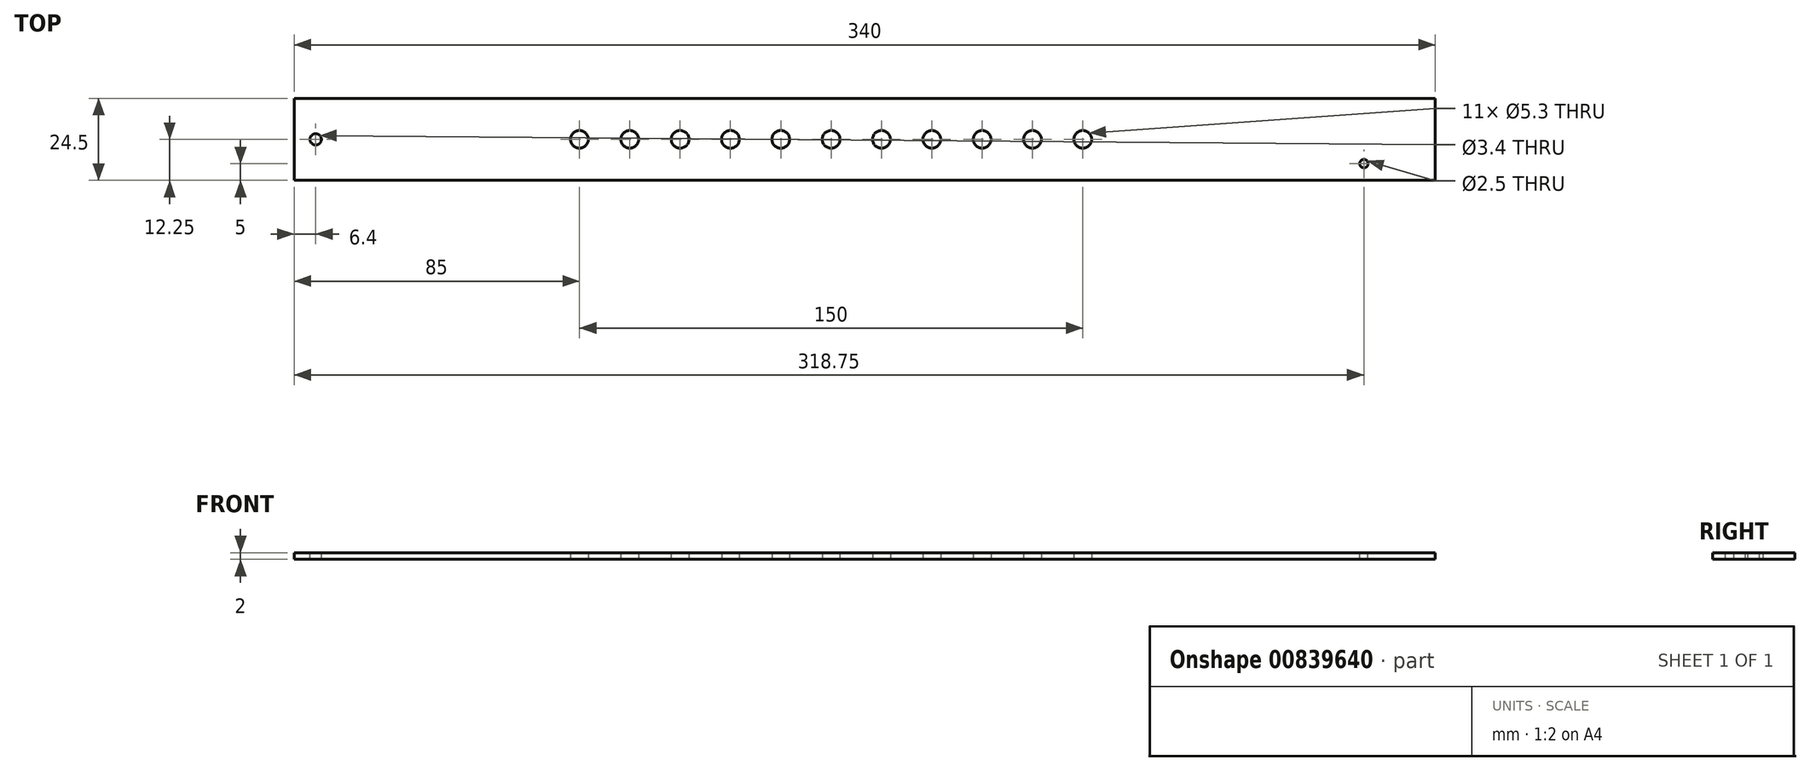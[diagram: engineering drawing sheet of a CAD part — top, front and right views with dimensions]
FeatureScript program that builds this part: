
annotation { "Feature Type Name" : "Feature", "Feature Type Description" : "" }
export const myFeature = defineFeature(function(context is Context, id is Id, definition is map)
    precondition{}
    {
        {
            var Q0;
            Q0=qCreatedBy(makeId("Top.planeOp"),FACE);
            var sketch = newSketch(context, id + "F0", { "sketchPlane" : qUnion([Q0])});
            skLineSegment(sketch, "E0.bottom", {"start": v(150, -12.25) * mm, "end": v(-150, -12.25) * mm});
            skLineSegment(sketch, "E0.top", {"start": v(150, 12.25) * mm, "end": v(-150, 12.25) * mm});
            skLineSegment(sketch, "E0.left", {"start": v(150, -12.25) * mm, "end": v(150, 12.25) * mm});
            skLineSegment(sketch, "E0.right", {"start": v(-150, -12.25) * mm, "end": v(-150, 12.25) * mm});
            skPoint(sketch, "E0.middle", {"position": v(0, 0) * mm});
            skCircle(sketch, "E1.4.0.0", {"center": v(-75, 0) * mm, "radius": 2.65 * mm});
            skCircle(sketch, "E1.5.0.0", {"center": v(-60, 0) * mm, "radius": 2.65 * mm});
            skCircle(sketch, "E1.6.0.0", {"center": v(-45, 0) * mm, "radius": 2.65 * mm});
            skCircle(sketch, "E1.7.0.0", {"center": v(-30, 0) * mm, "radius": 2.65 * mm});
            skCircle(sketch, "E1.8.0.0", {"center": v(-15, 0) * mm, "radius": 2.65 * mm});
            skCircle(sketch, "E1.9.0.0", {"center": v(0, 0) * mm, "radius": 2.65 * mm});
            skCircle(sketch, "E1.10.0.0", {"center": v(15, 0) * mm, "radius": 2.65 * mm});
            skCircle(sketch, "E1.11.0.0", {"center": v(30, 0) * mm, "radius": 2.65 * mm});
            skCircle(sketch, "E1.12.0.0", {"center": v(45, 0) * mm, "radius": 2.65 * mm});
            skCircle(sketch, "E1.13.0.0", {"center": v(60, 0) * mm, "radius": 2.65 * mm});
            skCircle(sketch, "E1.14.0.0", {"center": v(75, 0) * mm, "radius": 2.65 * mm});
            skLineSegment(sketch, "E1.direction1", {"start": v(-135, 0) * mm, "end": v(-120, 0) * mm, "construction": true});
            skSolve(sketch);
        }
        {
            var Q0;
            Q0=makeQuery(id+"F0.imprint","IMPRINT",FACE,{"disambiguationData":[TD([[makeQuery(id+"F0.imprint","IMPRINT",EDGE,{"derivedFrom":sQuery(id+"F0.wireOp",EDGE,"E0.bottom")}),-1.0]])]});
            extrude(context, id + "F1", {"entities" : qUnion([Q0]), "depth" : 2 * mm, "offsetDistance" : 25 * mm});
        }
        {
            var Q0;
            Q0=makeQuery(id+"F1.opExtrude","SWEPT_FACE",FACE,{"disambiguationData":[OSD([sQuery(id+"F0.wireOp",EDGE,"E0.right")])]});
            extrude(context, id + "F2", {"entities" : qUnion([Q0]), "operationType" : NewBodyOperationType.ADD, "depth" : 10 * mm, "offsetDistance" : 25 * mm});
        }
        {
            var Q0;
            Q0=makeQuery(id+"F1.opExtrude","SWEPT_FACE",FACE,{"disambiguationData":[OSD([sQuery(id+"F0.wireOp",EDGE,"E0.left")])]});
            extrude(context, id + "F3", {"entities" : qUnion([Q0]), "operationType" : NewBodyOperationType.ADD, "depth" : 30 * mm, "offsetDistance" : 25 * mm});
        }
        {
            var Q0;
            {var subQ0=sQuery(id+"F0.wireOp",EDGE,"E0.left");var subQ1=sQuery(id+"F0.wireOp",EDGE,"E0.right");Q0=makeQuery(id+"F3.boolean.opBoolean","MERGE",FACE,{"derivedFrom":[makeQuery(id+"F2.boolean.opBoolean","MERGE",FACE,{"derivedFrom":[makeQuery(id+"F1.opExtrude","CAP_FACE",FACE,{"disambiguationData":[OSD([sQuery(id+"F0.wireOp",EDGE,"E0.bottom"),sQuery(id+"F0.wireOp",EDGE,"E0.top"),subQ0,subQ1,sQuery(id+"F0.wireOp",EDGE,"LckrCdrf-Oz9b-iWqB-HkfW-gHpTPrbceAxr"),sQuery(id+"F0.wireOp",EDGE,"E1.1.0.0"),sQuery(id+"F0.wireOp",EDGE,"E1.2.0.0"),sQuery(id+"F0.wireOp",EDGE,"E1.3.0.0"),sQuery(id+"F0.wireOp",EDGE,"E1.4.0.0"),sQuery(id+"F0.wireOp",EDGE,"E1.5.0.0"),sQuery(id+"F0.wireOp",EDGE,"E1.6.0.0"),sQuery(id+"F0.wireOp",EDGE,"E1.7.0.0"),sQuery(id+"F0.wireOp",EDGE,"E1.8.0.0"),sQuery(id+"F0.wireOp",EDGE,"E1.9.0.0"),sQuery(id+"F0.wireOp",EDGE,"E1.10.0.0"),sQuery(id+"F0.wireOp",EDGE,"E1.11.0.0"),sQuery(id+"F0.wireOp",EDGE,"E1.12.0.0"),sQuery(id+"F0.wireOp",EDGE,"E1.13.0.0"),sQuery(id+"F0.wireOp",EDGE,"E1.14.0.0"),sQuery(id+"F0.wireOp",EDGE,"E1.15.0.0"),sQuery(id+"F0.wireOp",EDGE,"E1.16.0.0"),sQuery(id+"F0.wireOp",EDGE,"E1.17.0.0"),sQuery(id+"F0.wireOp",EDGE,"E1.18.0.0")])],"isStart":false}),makeQuery(id+"F2.opExtrude","SWEPT_FACE",FACE,{"disambiguationData":[OSD([subQ1]),TDD([makeQuery(id+"F1.opExtrude","CAP_EDGE",EDGE,{"disambiguationData":[OSD([subQ1])],"isStart":false})])]})]}),makeQuery(id+"F3.opExtrude","SWEPT_FACE",FACE,{"disambiguationData":[OSD([subQ0]),TDD([makeQuery(id+"F1.opExtrude","CAP_EDGE",EDGE,{"disambiguationData":[OSD([subQ0])],"isStart":false})])]})]});}
            var sketch = newSketch(context, id + "F4", { "sketchPlane" : qUnion([Q0])});
            skCircle(sketch, "E2", {"center": v(-153.6, 0) * mm, "radius": 1.7 * mm});
            skSolve(sketch);
        }
        {
            var Q0;
            Q0=makeQuery(id+"F4.imprint","IMPRINT",FACE,{"disambiguationData":[TD([[makeQuery(id+"F4.imprint","IMPRINT",EDGE,{"derivedFrom":sQuery(id+"F4.wireOp",EDGE,"E2")}),1.0]])]});
            extrude(context, id + "F5", {"entities" : qUnion([Q0]), "operationType" : NewBodyOperationType.REMOVE, "endBound" : BoundingType.UP_TO_NEXT, "oppositeDirection" : true, "depth" : 25 * mm, "offsetDistance" : 25 * mm});
        }
        {
            var Q0;
            {var subQ0=sQuery(id+"F0.wireOp",EDGE,"E0.left");var subQ1=sQuery(id+"F0.wireOp",EDGE,"E0.right");Q0=makeQuery(id+"F3.boolean.opBoolean","MERGE",FACE,{"derivedFrom":[makeQuery(id+"F2.boolean.opBoolean","MERGE",FACE,{"derivedFrom":[makeQuery(id+"F1.opExtrude","CAP_FACE",FACE,{"disambiguationData":[OSD([sQuery(id+"F0.wireOp",EDGE,"E0.bottom"),sQuery(id+"F0.wireOp",EDGE,"E0.top"),subQ0,subQ1,sQuery(id+"F0.wireOp",EDGE,"LckrCdrf-Oz9b-iWqB-HkfW-gHpTPrbceAxr"),sQuery(id+"F0.wireOp",EDGE,"E1.1.0.0"),sQuery(id+"F0.wireOp",EDGE,"E1.2.0.0"),sQuery(id+"F0.wireOp",EDGE,"E1.3.0.0"),sQuery(id+"F0.wireOp",EDGE,"E1.4.0.0"),sQuery(id+"F0.wireOp",EDGE,"E1.5.0.0"),sQuery(id+"F0.wireOp",EDGE,"E1.6.0.0"),sQuery(id+"F0.wireOp",EDGE,"E1.7.0.0"),sQuery(id+"F0.wireOp",EDGE,"E1.8.0.0"),sQuery(id+"F0.wireOp",EDGE,"E1.9.0.0"),sQuery(id+"F0.wireOp",EDGE,"E1.10.0.0"),sQuery(id+"F0.wireOp",EDGE,"E1.11.0.0"),sQuery(id+"F0.wireOp",EDGE,"E1.12.0.0"),sQuery(id+"F0.wireOp",EDGE,"E1.13.0.0"),sQuery(id+"F0.wireOp",EDGE,"E1.14.0.0"),sQuery(id+"F0.wireOp",EDGE,"E1.15.0.0"),sQuery(id+"F0.wireOp",EDGE,"E1.16.0.0"),sQuery(id+"F0.wireOp",EDGE,"E1.17.0.0"),sQuery(id+"F0.wireOp",EDGE,"E1.18.0.0")])],"isStart":false}),makeQuery(id+"F2.opExtrude","SWEPT_FACE",FACE,{"disambiguationData":[OSD([subQ1]),TDD([makeQuery(id+"F1.opExtrude","CAP_EDGE",EDGE,{"disambiguationData":[OSD([subQ1])],"isStart":false})])]})]}),makeQuery(id+"F3.opExtrude","SWEPT_FACE",FACE,{"disambiguationData":[OSD([subQ0]),TDD([makeQuery(id+"F1.opExtrude","CAP_EDGE",EDGE,{"disambiguationData":[OSD([subQ0])],"isStart":false})])]})]});}
            var sketch = newSketch(context, id + "F6", { "sketchPlane" : qUnion([Q0])});
            skCircle(sketch, "E3", {"center": v(158.75, -7.25) * mm, "radius": 1.25 * mm});
            skSolve(sketch);
        }
        {
            var Q0;
            Q0=makeQuery(id+"F6.imprint","IMPRINT",FACE,{"disambiguationData":[TD([[makeQuery(id+"F6.imprint","IMPRINT",EDGE,{"derivedFrom":sQuery(id+"F6.wireOp",EDGE,"E3")}),1.0]])]});
            extrude(context, id + "F7", {"entities" : qUnion([Q0]), "operationType" : NewBodyOperationType.REMOVE, "endBound" : BoundingType.UP_TO_NEXT, "oppositeDirection" : true, "depth" : 25 * mm, "offsetDistance" : 25 * mm});
        }
    });
